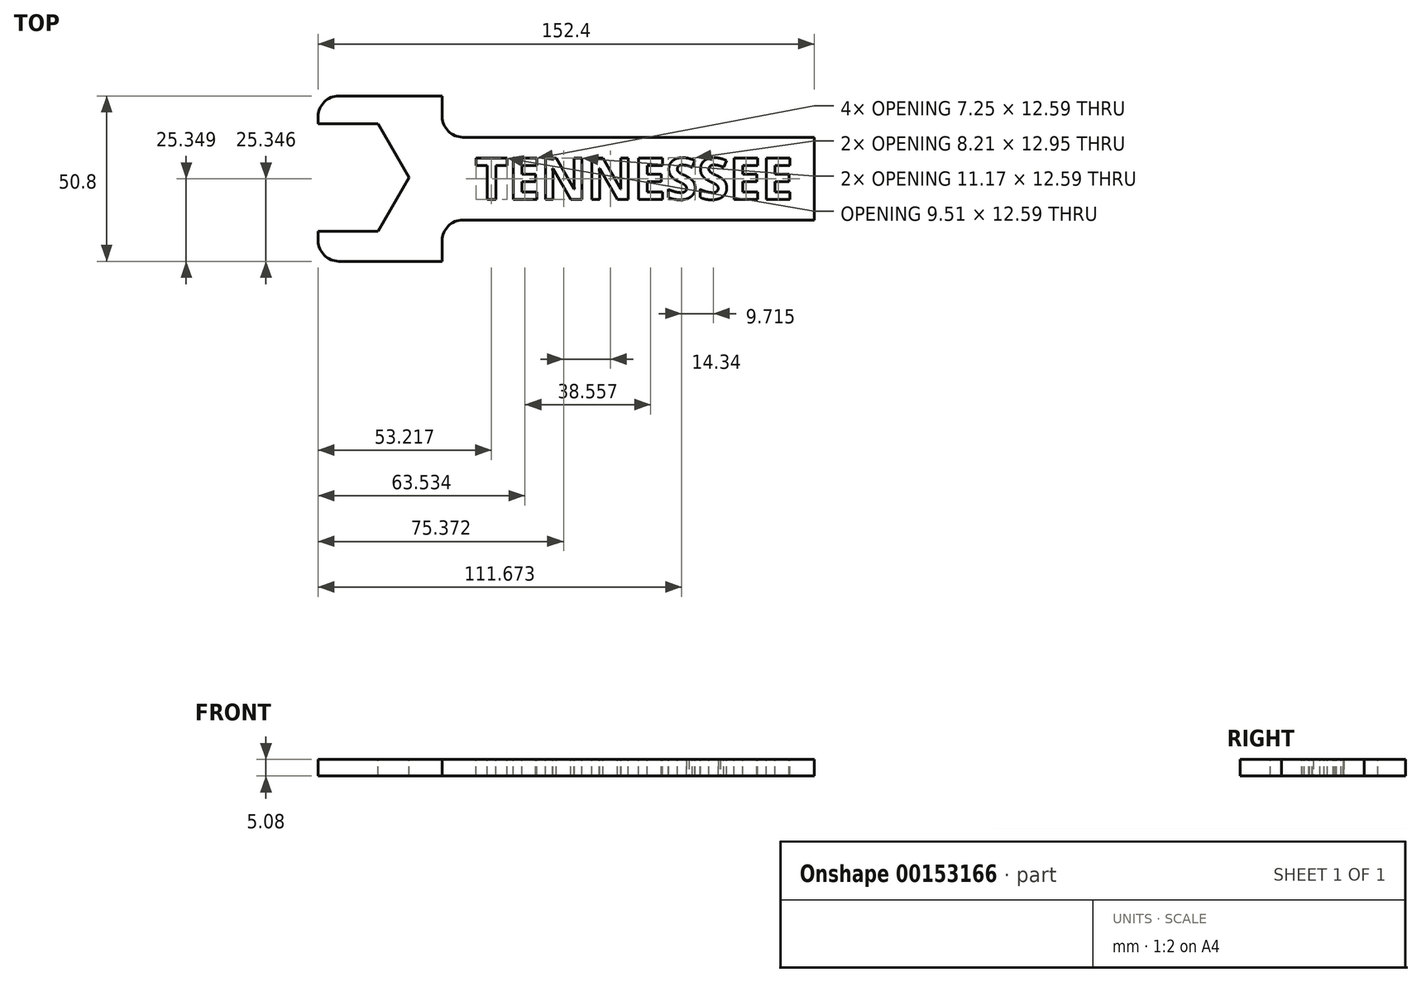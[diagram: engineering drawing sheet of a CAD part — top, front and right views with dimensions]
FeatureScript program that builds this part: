
annotation { "Feature Type Name" : "Feature", "Feature Type Description" : "" }
export const myFeature = defineFeature(function(context is Context, id is Id, definition is map)
    precondition{}
    {
        {
            var Q0;
            Q0=qCreatedBy(makeId("Top.planeOp"),FACE);
            var sketch = newSketch(context, id + "F0", { "sketchPlane" : qUnion([Q0])});
            skLineSegment(sketch, "E0", {"start": v(0, 0) * mm, "end": v(152.4, 0) * mm});
            skLineSegment(sketch, "E1", {"start": v(152.4, 0) * mm, "end": v(152.4, 50.8) * mm});
            skLineSegment(sketch, "E2", {"start": v(152.4, 50.8) * mm, "end": v(0, 50.8) * mm});
            skLineSegment(sketch, "E3", {"start": v(0, 50.8) * mm, "end": v(0, 0) * mm});
            skSolve(sketch);
        }
        {
            var Q0;
            Q0=makeQuery(id+"F0.imprint","IMPRINT",FACE,{"disambiguationData":[TD([[makeQuery(id+"F0.imprint","IMPRINT",EDGE,{"derivedFrom":sQuery(id+"F0.wireOp",EDGE,"E0")}),1.0]])]});
            extrude(context, id + "F1", {"entities" : qUnion([Q0]), "depth" : 5.08 * mm});
        }
        {
            var Q0;
            Q0=makeQuery(id+"F1.opExtrude","CAP_FACE",FACE,{"disambiguationData":[OSD([sQuery(id+"F0.wireOp",EDGE,"E0"),sQuery(id+"F0.wireOp",EDGE,"E1"),sQuery(id+"F0.wireOp",EDGE,"E2"),sQuery(id+"F0.wireOp",EDGE,"E3")])],"isStart":false});
            var sketch = newSketch(context, id + "F2", { "sketchPlane" : qUnion([Q0])});
            skCircle(sketch, "E4.cCircle", {"center": v(8.89, 25.75) * mm, "radius": 16.51 * mm, "construction": true});
            skLineSegment(sketch, "E4.0", {"start": v(18.42, 42.26) * mm, "end": v(27.95, 25.75) * mm});
            skLineSegment(sketch, "E4.1", {"start": v(27.95, 25.75) * mm, "end": v(18.42, 9.24) * mm});
            skLineSegment(sketch, "E4.2", {"start": v(18.42, 9.24) * mm, "end": v(-0.64, 9.24) * mm});
            skLineSegment(sketch, "E4.3", {"start": v(-0.64, 9.24) * mm, "end": v(-10.17, 25.75) * mm});
            skLineSegment(sketch, "E4.4", {"start": v(-10.17, 25.75) * mm, "end": v(-0.64, 42.26) * mm});
            skLineSegment(sketch, "E4.5", {"start": v(-0.64, 42.26) * mm, "end": v(18.42, 42.26) * mm});
            skPoint(sketch, "E4.0.midPoint", {"position": v(23.19, 34) * mm});
            skSolve(sketch);
        }
        {
            var Q0;
            {var subQ1=sQuery(id+"F2.wireOp",EDGE,"E4.0");Q0=makeQuery(id+"F2.imprint","IMPRINT",FACE,{"disambiguationData":[TD([[makeQuery(id+"F2.imprint","IMPRINT",EDGE,{"derivedFrom":subQ1}),-1.0]])]});}
            extrude(context, id + "F3", {"entities" : qUnion([Q0]), "operationType" : NewBodyOperationType.REMOVE, "endBound" : BoundingType.THROUGH_ALL, "oppositeDirection" : true, "depth" : 25.4 * mm});
        }
        {
            var Q0;
            Q0=makeQuery(id+"F1.opExtrude","CAP_FACE",FACE,{"disambiguationData":[OSD([sQuery(id+"F0.wireOp",EDGE,"E0"),sQuery(id+"F0.wireOp",EDGE,"E1"),sQuery(id+"F0.wireOp",EDGE,"E2"),sQuery(id+"F0.wireOp",EDGE,"E3")])],"isStart":false});
            var sketch = newSketch(context, id + "F4", { "sketchPlane" : qUnion([Q0])});
            skLineSegment(sketch, "E5.bottom", {"start": v(38.1, 50.8) * mm, "end": v(152.4, 50.8) * mm});
            skLineSegment(sketch, "E5.top", {"start": v(38.1, 38.1) * mm, "end": v(152.4, 38.1) * mm});
            skLineSegment(sketch, "E5.left", {"start": v(38.1, 50.8) * mm, "end": v(38.1, 38.1) * mm});
            skLineSegment(sketch, "E5.right", {"start": v(152.4, 50.8) * mm, "end": v(152.4, 38.1) * mm});
            skLineSegment(sketch, "E6.bottom", {"start": v(152.4, 0) * mm, "end": v(38.1, 0) * mm});
            skLineSegment(sketch, "E6.top", {"start": v(152.4, 12.7) * mm, "end": v(38.1, 12.7) * mm});
            skLineSegment(sketch, "E6.left", {"start": v(152.4, 0) * mm, "end": v(152.4, 12.7) * mm});
            skLineSegment(sketch, "E6.right", {"start": v(38.1, 0) * mm, "end": v(38.1, 12.7) * mm});
            skSolve(sketch);
        }
        {
            var Q0;
            Q0=makeQuery(id+"F4.imprint","IMPRINT",FACE,{"disambiguationData":[TD([[makeQuery(id+"F4.imprint","IMPRINT",EDGE,{"derivedFrom":sQuery(id+"F4.wireOp",EDGE,"E5.bottom")}),1.0]])]});
            var Q1;
            Q1=makeQuery(id+"F4.imprint","IMPRINT",FACE,{"disambiguationData":[TD([[makeQuery(id+"F4.imprint","IMPRINT",EDGE,{"derivedFrom":sQuery(id+"F4.wireOp",EDGE,"E6.bottom")}),1.0]])]});
            extrude(context, id + "F5", {"entities" : qUnion([Q0, Q1]), "operationType" : NewBodyOperationType.REMOVE, "endBound" : BoundingType.THROUGH_ALL, "oppositeDirection" : true, "depth" : 25.4 * mm});
        }
        {
            var Q0;
            Q0=makeQuery(id+"F5.boolean.opBoolean","COPY",EDGE,{"derivedFrom":makeQuery(id+"F5.opExtrude","SWEPT_EDGE",EDGE,{"disambiguationData":[OSD([sQuery(id+"F0.wireOp",EDGE,"E0"),sQuery(id+"F4.wireOp",EDGE,"E6.bottom"),sQuery(id+"F4.wireOp",EDGE,"E6.right")])]})});
            var Q1;
            Q1=makeQuery(id+"F5.boolean.opBoolean","COPY",EDGE,{"derivedFrom":makeQuery(id+"F5.opExtrude","SWEPT_EDGE",EDGE,{"disambiguationData":[OSD([sQuery(id+"F0.wireOp",EDGE,"E1"),sQuery(id+"F4.wireOp",EDGE,"E6.top"),sQuery(id+"F4.wireOp",EDGE,"E6.left")])]})});
            var Q2;
            Q2=makeQuery(id+"F5.boolean.opBoolean","COPY",EDGE,{"derivedFrom":makeQuery(id+"F5.opExtrude","SWEPT_EDGE",EDGE,{"disambiguationData":[OSD([sQuery(id+"F0.wireOp",EDGE,"E1"),sQuery(id+"F4.wireOp",EDGE,"E5.top"),sQuery(id+"F4.wireOp",EDGE,"E5.right")])]})});
            var Q3;
            Q3=makeQuery(id+"F5.boolean.opBoolean","COPY",EDGE,{"derivedFrom":makeQuery(id+"F5.opExtrude","SWEPT_EDGE",EDGE,{"disambiguationData":[OSD([sQuery(id+"F4.wireOp",EDGE,"E5.top"),sQuery(id+"F4.wireOp",EDGE,"E5.left")])]})});
            var Q4;
            Q4=makeQuery(id+"F1.opExtrude","SWEPT_EDGE",EDGE,{"disambiguationData":[OSD([sQuery(id+"F0.wireOp",EDGE,"E2"),sQuery(id+"F0.wireOp",EDGE,"E3")])]});
            var Q5;
            Q5=makeQuery(id+"F1.opExtrude","SWEPT_EDGE",EDGE,{"disambiguationData":[OSD([sQuery(id+"F0.wireOp",EDGE,"E0"),sQuery(id+"F0.wireOp",EDGE,"E3")])]});
            var Q6;
            Q6=makeQuery(id+"F5.boolean.opBoolean","COPY",EDGE,{"derivedFrom":makeQuery(id+"F5.opExtrude","SWEPT_EDGE",EDGE,{"disambiguationData":[OSD([sQuery(id+"F4.wireOp",EDGE,"E6.top"),sQuery(id+"F4.wireOp",EDGE,"E6.right")])]})});
            var Q7;
            Q7=makeQuery(id+"F5.boolean.opBoolean","COPY",EDGE,{"derivedFrom":makeQuery(id+"F5.opExtrude","SWEPT_EDGE",EDGE,{"disambiguationData":[OSD([sQuery(id+"F0.wireOp",EDGE,"E2"),sQuery(id+"F4.wireOp",EDGE,"E5.bottom"),sQuery(id+"F4.wireOp",EDGE,"E5.left")])]})});
            fillet(context, id + "F6", {"entities" : qUnion([Q0, Q1, Q2, Q3, Q4, Q5, Q6, Q7]), "radius" : 6.35 * mm, "tangentPropagation" : true, "allowEdgeOverflow" : false});
        }
        {
            var Q0;
            Q0=makeQuery(id+"F1.opExtrude","CAP_FACE",FACE,{"disambiguationData":[OSD([sQuery(id+"F0.wireOp",EDGE,"E0"),sQuery(id+"F0.wireOp",EDGE,"E1"),sQuery(id+"F0.wireOp",EDGE,"E2"),sQuery(id+"F0.wireOp",EDGE,"E3")])],"isStart":false});
            var sketch = newSketch(context, id + "F7", { "sketchPlane" : qUnion([Q0])});
            skText(sketch, "E7", { "text": "TENNESSEE", "fontName": "OpenSans-Bold.ttf"});
            const initialGuessF7  = {"E7": [0.04811, 0.01905, 1, 0, 0.0127]};
            skSetInitialGuess(sketch, initialGuessF7);
            skSolve(sketch);
        }
        {
            var Q0;
            Q0 = qSketchRegion(id + "F7", true);
            extrude(context, id + "F8", {"entities" : qUnion([Q0]), "operationType" : NewBodyOperationType.REMOVE, "endBound" : BoundingType.THROUGH_ALL, "oppositeDirection" : true, "depth" : 25.4 * mm});
        }
    });
